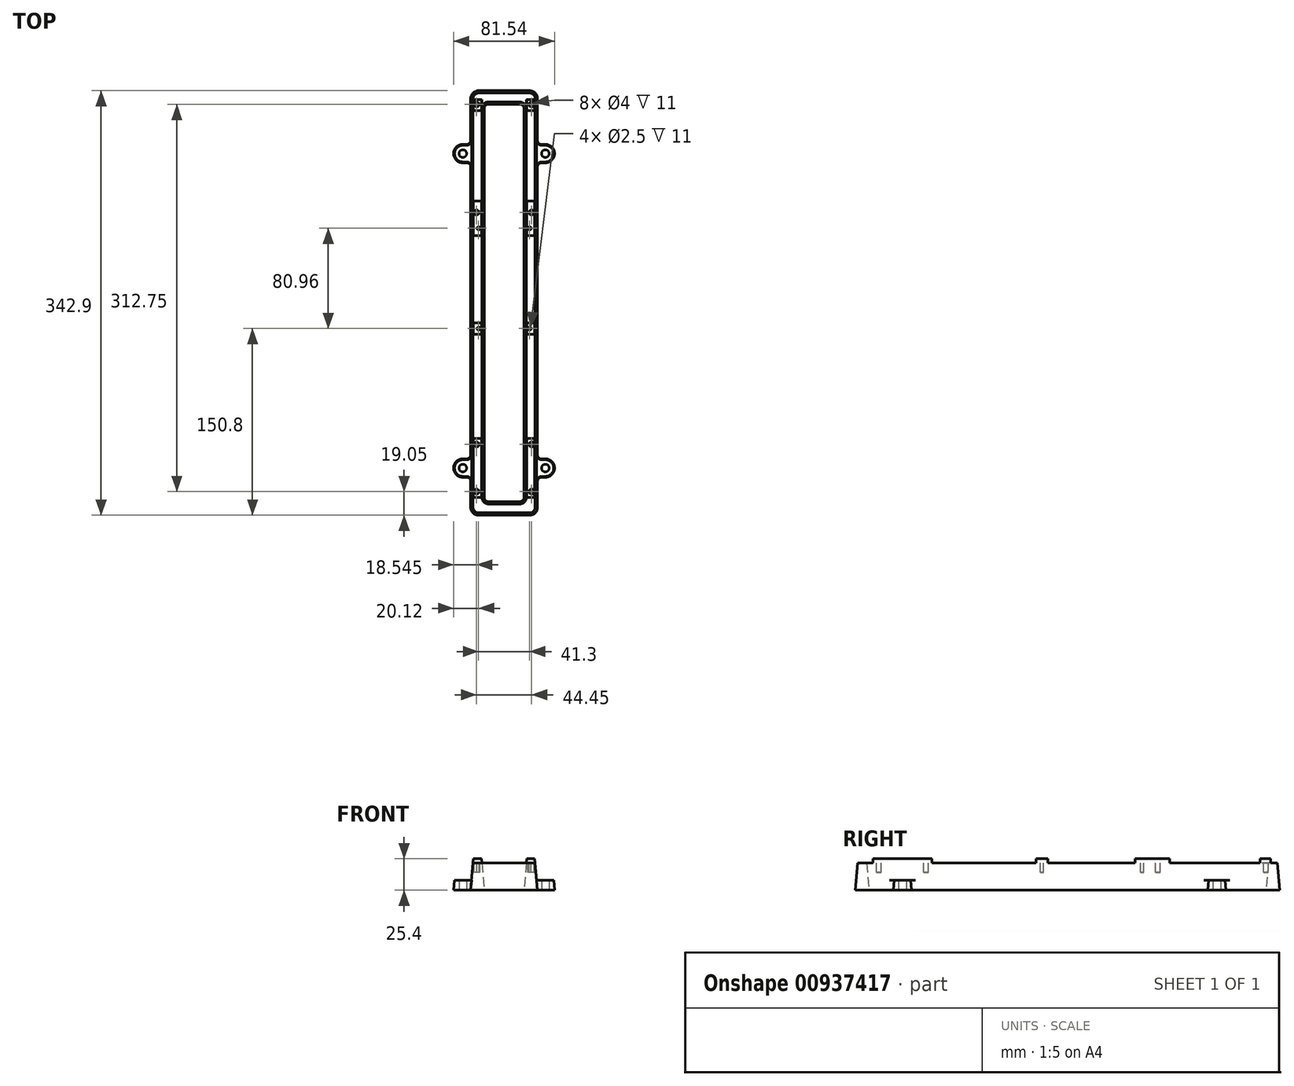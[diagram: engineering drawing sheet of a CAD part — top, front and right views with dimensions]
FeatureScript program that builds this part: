
annotation { "Feature Type Name" : "Feature", "Feature Type Description" : "" }
export const myFeature = defineFeature(function(context is Context, id is Id, definition is map)
    precondition{}
    {
        {
            var Q0;
            Q0=qCreatedBy(makeId("Top.planeOp"),FACE);
            var sketch = newSketch(context, id + "F0", { "sketchPlane" : qUnion([Q0])});
            skLineSegment(sketch, "E0", {"start": v(-33.35, 0) * mm, "end": v(33.35, 0) * mm, "construction": true});
            skLineSegment(sketch, "E1", {"start": v(0, -38.1) * mm, "end": v(0, 304.8) * mm, "construction": true});
            skLineSegment(sketch, "E2", {"start": v(-33.35, 254) * mm, "end": v(33.35, 254) * mm, "construction": true});
            skLineSegment(sketch, "E3.bottom", {"start": v(-20.65, 304.8) * mm, "end": v(20.65, 304.8) * mm});
            skLineSegment(sketch, "E3.top", {"start": v(-20.65, -38.1) * mm, "end": v(20.65, -38.1) * mm});
            skLineSegment(sketch, "E3.left", {"start": v(-27, 298.45) * mm, "end": v(-27, 264.62) * mm});
            skLineSegment(sketch, "E3.right", {"start": v(27, 298.45) * mm, "end": v(27, 264.62) * mm});
            skLineSegment(sketch, "E4.bottom", {"start": v(-12.8, 293.8) * mm, "end": v(12.8, 293.8) * mm});
            skLineSegment(sketch, "E4.top", {"start": v(-12.8, -27.1) * mm, "end": v(12.8, -27.1) * mm});
            skLineSegment(sketch, "E4.left", {"start": v(-16, 290.6) * mm, "end": v(-16, -23.9) * mm});
            skLineSegment(sketch, "E4.right", {"start": v(16, 290.6) * mm, "end": v(16, -23.9) * mm});
            skLineSegment(sketch, "E5", {"start": v(-30.2, 261.43) * mm, "end": v(-33.35, 261.43) * mm});
            skLineSegment(sketch, "E6", {"start": v(-33.35, 246.57) * mm, "end": v(-30.2, 246.57) * mm});
            skLineSegment(sketch, "E7", {"start": v(30.2, 246.57) * mm, "end": v(33.35, 246.57) * mm});
            skLineSegment(sketch, "E8", {"start": v(33.35, 261.43) * mm, "end": v(30.2, 261.43) * mm});
            skLineSegment(sketch, "E9.trimOffspring", {"start": v(-27, 243.37) * mm, "end": v(-27, 10.62) * mm});
            skLineSegment(sketch, "E10.trimOffspring", {"start": v(27, 243.37) * mm, "end": v(27, 10.62) * mm});
            skArc(sketch, "E11", {"start": v(-33.35, 261.43) * mm, "mid": v(-40.78, 254) * mm, "end": v(-33.35, 246.57) * mm});
            skPoint(sketch, "E12.end.orphan", {"position": v(-39.7, 246.57) * mm});
            skArc(sketch, "E13", {"start": v(33.35, 246.57) * mm, "mid": v(40.78, 254) * mm, "end": v(33.35, 261.43) * mm});
            skLineSegment(sketch, "E14", {"start": v(-33.35, 7.42) * mm, "end": v(-30.2, 7.42) * mm});
            skLineSegment(sketch, "E15", {"start": v(30.2, 7.42) * mm, "end": v(33.35, 7.43) * mm});
            skLineSegment(sketch, "E16", {"start": v(33.35, -7.43) * mm, "end": v(30.2, -7.43) * mm});
            skLineSegment(sketch, "E17", {"start": v(-30.2, -7.42) * mm, "end": v(-33.35, -7.42) * mm});
            skArc(sketch, "E18", {"start": v(-33.35, -7.42) * mm, "mid": v(-40.78, 0) * mm, "end": v(-33.35, 7.42) * mm});
            skArc(sketch, "E19", {"start": v(33.35, 7.43) * mm, "mid": v(40.78, 0) * mm, "end": v(33.35, -7.43) * mm});
            skLineSegment(sketch, "E20.trimOffspring", {"start": v(-27, -10.62) * mm, "end": v(-27, -31.75) * mm});
            skLineSegment(sketch, "E21.trimOffspring", {"start": v(27, -10.62) * mm, "end": v(27, -31.75) * mm});
            skPoint(sketch, "E22.visualSharp", {"position": v(27, -38.1) * mm});
            skArc(sketch, "E22.filletArc", {"start": v(20.65, -38.1) * mm, "mid": v(25.14, -36.24) * mm, "end": v(27, -31.75) * mm});
            skPoint(sketch, "E23.visualSharp", {"position": v(-27, -38.1) * mm});
            skArc(sketch, "E23.filletArc", {"start": v(-27, -31.75) * mm, "mid": v(-25.14, -36.24) * mm, "end": v(-20.65, -38.1) * mm});
            skPoint(sketch, "E24.visualSharp", {"position": v(-27, 304.8) * mm});
            skArc(sketch, "E24.filletArc", {"start": v(-20.65, 304.8) * mm, "mid": v(-25.14, 302.94) * mm, "end": v(-27, 298.45) * mm});
            skPoint(sketch, "E25.visualSharp", {"position": v(27, 304.8) * mm});
            skArc(sketch, "E25.filletArc", {"start": v(27, 298.45) * mm, "mid": v(25.14, 302.94) * mm, "end": v(20.65, 304.8) * mm});
            skPoint(sketch, "E26.visualSharp", {"position": v(16, 293.8) * mm});
            skArc(sketch, "E26.filletArc", {"start": v(16, 290.6) * mm, "mid": v(15.06, 292.86) * mm, "end": v(12.8, 293.8) * mm});
            skPoint(sketch, "E27.visualSharp", {"position": v(-16, 293.8) * mm});
            skArc(sketch, "E27.filletArc", {"start": v(-12.8, 293.8) * mm, "mid": v(-15.06, 292.86) * mm, "end": v(-16, 290.6) * mm});
            skPoint(sketch, "E28.visualSharp", {"position": v(-27, 246.57) * mm});
            skArc(sketch, "E28.filletArc", {"start": v(-27, 243.37) * mm, "mid": v(-27.94, 245.64) * mm, "end": v(-30.2, 246.57) * mm});
            skPoint(sketch, "E29.visualSharp", {"position": v(-27, 261.43) * mm});
            skArc(sketch, "E29.filletArc", {"start": v(-30.2, 261.43) * mm, "mid": v(-27.94, 262.36) * mm, "end": v(-27, 264.62) * mm});
            skPoint(sketch, "E30.visualSharp", {"position": v(27, 261.43) * mm});
            skArc(sketch, "E30.filletArc", {"start": v(27, 264.62) * mm, "mid": v(27.94, 262.36) * mm, "end": v(30.2, 261.43) * mm});
            skPoint(sketch, "E31.visualSharp", {"position": v(27, 246.57) * mm});
            skArc(sketch, "E31.filletArc", {"start": v(30.2, 246.57) * mm, "mid": v(27.94, 245.64) * mm, "end": v(27, 243.37) * mm});
            skPoint(sketch, "E32.visualSharp", {"position": v(-16, -27.1) * mm});
            skArc(sketch, "E32.filletArc", {"start": v(-16, -23.9) * mm, "mid": v(-15.06, -26.16) * mm, "end": v(-12.8, -27.1) * mm});
            skPoint(sketch, "E33.visualSharp", {"position": v(16, -27.1) * mm});
            skArc(sketch, "E33.filletArc", {"start": v(12.8, -27.1) * mm, "mid": v(15.06, -26.16) * mm, "end": v(16, -23.9) * mm});
            skPoint(sketch, "E34.visualSharp", {"position": v(27, -7.43) * mm});
            skArc(sketch, "E34.filletArc", {"start": v(30.2, -7.43) * mm, "mid": v(27.94, -8.36) * mm, "end": v(27, -10.62) * mm});
            skPoint(sketch, "E35.visualSharp", {"position": v(27, 7.42) * mm});
            skArc(sketch, "E35.filletArc", {"start": v(27, 10.62) * mm, "mid": v(27.94, 8.36) * mm, "end": v(30.2, 7.43) * mm});
            skPoint(sketch, "E36.visualSharp", {"position": v(-27, 7.42) * mm});
            skArc(sketch, "E36.filletArc", {"start": v(-30.2, 7.43) * mm, "mid": v(-27.94, 8.36) * mm, "end": v(-27, 10.62) * mm});
            skPoint(sketch, "E37.visualSharp", {"position": v(-27, -7.42) * mm});
            skArc(sketch, "E37.filletArc", {"start": v(-27, -10.62) * mm, "mid": v(-27.94, -8.36) * mm, "end": v(-30.2, -7.42) * mm});
            skSolve(sketch);
        }
        {
            var Q0;
            Q0 = qSketchRegion(id + "F0", true);
            extrude(context, id + "F1", {"entities" : qUnion([Q0]), "depth" : 25.4 * mm, "offsetDistance" : 25 * mm, "hasDraft" : true, "draftAngle" : 5 * degree, "draftPullDirection" : true});
        }
        {
            var Q0;
            Q0=qCreatedBy(makeId("Front.planeOp"),FACE);
            var sketch = newSketch(context, id + "F2", { "sketchPlane" : qUnion([Q0])});
            skLineSegment(sketch, "E38.0", {"start": v(-24.78, 25.4) * mm, "end": v(-26.3, 8.1) * mm});
            skLineSegment(sketch, "E39.0", {"start": v(24.78, 25.4) * mm, "end": v(26.3, 8.1) * mm});
            skLineSegment(sketch, "E40.0", {"start": v(-38.55, 25.4) * mm, "end": v(-24.78, 25.4) * mm});
            skLineSegment(sketch, "E41", {"start": v(38.55, 25.4) * mm, "end": v(40.07, 8.1) * mm});
            skLineSegment(sketch, "E42", {"start": v(-40.07, 8.1) * mm, "end": v(-38.55, 25.4) * mm});
            skLineSegment(sketch, "E43", {"start": v(40.07, 8.1) * mm, "end": v(26.3, 8.1) * mm});
            skPoint(sketch, "E44.orphan", {"position": v(27, 0) * mm});
            skLineSegment(sketch, "E45.trimOffspring", {"start": v(-26.3, 8.1) * mm, "end": v(-40.07, 8.1) * mm});
            skPoint(sketch, "E46.orphan", {"position": v(-27, 0) * mm});
            skPoint(sketch, "E47.orphan", {"position": v(-20.65, 25.4) * mm});
            skPoint(sketch, "E48.orphan", {"position": v(20.65, 25.4) * mm});
            skLineSegment(sketch, "E49.trimOffspring", {"start": v(24.78, 25.4) * mm, "end": v(38.55, 25.4) * mm});
            skSolve(sketch);
        }
        {
            var Q0;
            Q0 = qSketchRegion(id + "F2", true);
            extrude(context, id + "F3", {"entities" : qUnion([Q0]), "operationType" : NewBodyOperationType.REMOVE, "endBound" : BoundingType.THROUGH_ALL, "oppositeDirection" : true, "depth" : 25 * mm, "offsetDistance" : 25 * mm, "hasSecondDirection" : true, "secondDirectionBound" : SecondDirectionBoundingType.THROUGH_ALL, "secondDirectionOppositeDirection" : false, "secondDirectionDepth" : 25 * mm});
        }
        {
            var Q0;
            Q0=qCreatedBy(makeId("Right.planeOp"),FACE);
            var sketch = newSketch(context, id + "F4", { "sketchPlane" : qUnion([Q0])});
            skLineSegment(sketch, "E50.0", {"start": v(187.8, 25.4) * mm, "end": v(117.38, 25.4) * mm});
            skLineSegment(sketch, "E51", {"start": v(-23.8, 25.4) * mm, "end": v(-23.8, 22) * mm});
            skLineSegment(sketch, "E52", {"start": v(-23.8, 22) * mm, "end": v(-36.18, 22) * mm});
            skLineSegment(sketch, "E53", {"start": v(23.8, 25.4) * mm, "end": v(23.8, 22) * mm});
            skLineSegment(sketch, "E54", {"start": v(23.8, 22) * mm, "end": v(108.03, 22) * mm});
            skLineSegment(sketch, "E55", {"start": v(0, 25.4) * mm, "end": v(0, 0) * mm, "construction": true});
            skLineSegment(sketch, "E56.0", {"start": v(-35.88, 25.4) * mm, "end": v(-36.18, 22) * mm});
            skPoint(sketch, "E57.orphan", {"position": v(-38.1, 0) * mm});
            skPoint(sketch, "E58.orphan", {"position": v(-31.75, 25.4) * mm});
            skLineSegment(sketch, "E59.trimOffspring", {"start": v(-23.8, 25.4) * mm, "end": v(-35.88, 25.4) * mm});
            skLineSegment(sketch, "E60", {"start": v(112.7, 25.4) * mm, "end": v(112.7, 0) * mm, "construction": true});
            skLineSegment(sketch, "E61", {"start": v(117.38, 25.4) * mm, "end": v(117.38, 22) * mm});
            skLineSegment(sketch, "E62", {"start": v(108.03, 22) * mm, "end": v(108.03, 25.4) * mm});
            skLineSegment(sketch, "E63", {"start": v(108.03, 25.4) * mm, "end": v(23.8, 25.4) * mm});
            skLineSegment(sketch, "E64", {"start": v(187.8, 22) * mm, "end": v(117.38, 22) * mm});
            skLineSegment(sketch, "E65", {"start": v(187.8, 22) * mm, "end": v(187.8, 25.4) * mm});
            skPoint(sketch, "E66.orphan", {"position": v(298.45, 25.4) * mm});
            skLineSegment(sketch, "E67", {"start": v(206.4, 25.52) * mm, "end": v(206.4, 0) * mm, "construction": true});
            skSolve(sketch);
        }
        {
            var Q0;
            Q0 = qSketchRegion(id + "F4", true);
            extrude(context, id + "F5", {"entities" : qUnion([Q0]), "operationType" : NewBodyOperationType.REMOVE, "endBound" : BoundingType.THROUGH_ALL, "oppositeDirection" : true, "depth" : 25 * mm, "offsetDistance" : 25 * mm, "hasSecondDirection" : true, "secondDirectionBound" : SecondDirectionBoundingType.THROUGH_ALL, "secondDirectionOppositeDirection" : false, "secondDirectionDepth" : 25 * mm});
        }
        {
            var Q0;
            Q0=qCreatedBy(makeId("Right.planeOp"),FACE);
            var sketch = newSketch(context, id + "F6", { "sketchPlane" : qUnion([Q0])});
            skLineSegment(sketch, "E68.0", {"start": v(187.8, 22) * mm, "end": v(117.38, 22) * mm});
            skLineSegment(sketch, "E69.0", {"start": v(302.58, 25.4) * mm, "end": v(297.5, 25.4) * mm});
            skLineSegment(sketch, "E70", {"start": v(215.8, 25.4) * mm, "end": v(215.8, 22) * mm});
            skLineSegment(sketch, "E71", {"start": v(297.5, 25.4) * mm, "end": v(297.5, 22) * mm});
            skLineSegment(sketch, "E72", {"start": v(302.88, 22) * mm, "end": v(297.5, 22) * mm});
            skLineSegment(sketch, "E73", {"start": v(288.8, 22) * mm, "end": v(288.8, 25.4) * mm});
            skPoint(sketch, "E74.orphan", {"position": v(298.45, 25.4) * mm});
            skLineSegment(sketch, "E75.trimOffspring", {"start": v(288.8, 25.4) * mm, "end": v(187.8, 25.4) * mm});
            skLineSegment(sketch, "E76.trimOffspring", {"start": v(288.8, 22) * mm, "end": v(215.8, 22) * mm});
            skLineSegment(sketch, "E77.0", {"start": v(302.58, 25.4) * mm, "end": v(302.88, 22) * mm});
            skPoint(sketch, "E78.orphan", {"position": v(304.8, 0) * mm});
            skLineSegment(sketch, "E79", {"start": v(293.7, 25.53) * mm, "end": v(293.7, 22) * mm, "construction": true});
            skSolve(sketch);
        }
        {
            var Q0;
            Q0 = qSketchRegion(id + "F6", true);
            extrude(context, id + "F7", {"entities" : qUnion([Q0]), "operationType" : NewBodyOperationType.REMOVE, "endBound" : BoundingType.THROUGH_ALL, "oppositeDirection" : true, "depth" : 25 * mm, "offsetDistance" : 25 * mm, "hasSecondDirection" : true, "secondDirectionBound" : SecondDirectionBoundingType.THROUGH_ALL, "secondDirectionOppositeDirection" : false, "secondDirectionDepth" : 25 * mm});
        }
        {
            var Q0;
            {var subQ2=sQuery(id+"F0.wireOp",EDGE,"E3.left");Q0=makeQuery(id+"F7.boolean.opBoolean","COPY",FACE,{"disambiguationData":[TD([makeQuery(id+"F1.opExtrude","SWEPT_FACE",FACE,{"disambiguationData":[OSD([subQ2])]})])],"derivedFrom":makeQuery(id+"F7.opExtrude","SWEPT_FACE",FACE,{"disambiguationData":[OSD([sQuery(id+"F6.wireOp",EDGE,"E73")])]})});}
            var sketch = newSketch(context, id + "F8", { "sketchPlane" : qUnion([Q0])});
            skLineSegment(sketch, "E80.0", {"start": v(-17.92, 22) * mm, "end": v(-18.22, 25.4) * mm});
            skLineSegment(sketch, "E81.0", {"start": v(17.92, 22) * mm, "end": v(18.22, 25.4) * mm});
            skLineSegment(sketch, "E82.0", {"start": v(-18.22, 25.4) * mm, "end": v(18.22, 25.4) * mm});
            skLineSegment(sketch, "E83.0", {"start": v(-17.92, 22) * mm, "end": v(17.92, 22) * mm});
            skPoint(sketch, "E84.orphan", {"position": v(-20.65, 22) * mm});
            skPoint(sketch, "E85.orphan", {"position": v(20.65, 22) * mm});
            skPoint(sketch, "E86.orphan", {"position": v(12.8, 25.4) * mm});
            skPoint(sketch, "E87.orphan", {"position": v(-12.8, 25.4) * mm});
            skSolve(sketch);
        }
        {
            var Q0;
            Q0 = qSketchRegion(id + "F8", true);
            extrude(context, id + "F9", {"entities" : qUnion([Q0]), "operationType" : NewBodyOperationType.REMOVE, "endBound" : BoundingType.THROUGH_ALL, "oppositeDirection" : true, "depth" : 25 * mm, "offsetDistance" : 25 * mm});
        }
        {
            var Q0;
            Q0=makeQuery(id+"F1.opExtrude","CAP_FACE",FACE,{"disambiguationData":[OSD([sQuery(id+"F0.wireOp",EDGE,"E3.bottom"),sQuery(id+"F0.wireOp",EDGE,"E3.top"),sQuery(id+"F0.wireOp",EDGE,"E3.left"),sQuery(id+"F0.wireOp",EDGE,"E3.right"),sQuery(id+"F0.wireOp",EDGE,"E4.bottom"),sQuery(id+"F0.wireOp",EDGE,"E4.top"),sQuery(id+"F0.wireOp",EDGE,"E4.left"),sQuery(id+"F0.wireOp",EDGE,"E4.right"),sQuery(id+"F0.wireOp",EDGE,"E5"),sQuery(id+"F0.wireOp",EDGE,"E6"),sQuery(id+"F0.wireOp",EDGE,"E7"),sQuery(id+"F0.wireOp",EDGE,"E8"),sQuery(id+"F0.wireOp",EDGE,"E9.trimOffspring"),sQuery(id+"F0.wireOp",EDGE,"E10.trimOffspring"),sQuery(id+"F0.wireOp",EDGE,"E11"),sQuery(id+"F0.wireOp",EDGE,"E13"),sQuery(id+"F0.wireOp",EDGE,"E14"),sQuery(id+"F0.wireOp",EDGE,"E15"),sQuery(id+"F0.wireOp",EDGE,"E16"),sQuery(id+"F0.wireOp",EDGE,"E17"),sQuery(id+"F0.wireOp",EDGE,"E18"),sQuery(id+"F0.wireOp",EDGE,"E19"),sQuery(id+"F0.wireOp",EDGE,"E20.trimOffspring"),sQuery(id+"F0.wireOp",EDGE,"E21.trimOffspring"),sQuery(id+"F0.wireOp",EDGE,"E22.filletArc"),sQuery(id+"F0.wireOp",EDGE,"E23.filletArc"),sQuery(id+"F0.wireOp",EDGE,"E24.filletArc"),sQuery(id+"F0.wireOp",EDGE,"E25.filletArc"),sQuery(id+"F0.wireOp",EDGE,"E26.filletArc"),sQuery(id+"F0.wireOp",EDGE,"E27.filletArc"),sQuery(id+"F0.wireOp",EDGE,"E28.filletArc"),sQuery(id+"F0.wireOp",EDGE,"E29.filletArc"),sQuery(id+"F0.wireOp",EDGE,"E30.filletArc"),sQuery(id+"F0.wireOp",EDGE,"E31.filletArc"),sQuery(id+"F0.wireOp",EDGE,"E32.filletArc"),sQuery(id+"F0.wireOp",EDGE,"E33.filletArc"),sQuery(id+"F0.wireOp",EDGE,"E34.filletArc"),sQuery(id+"F0.wireOp",EDGE,"E35.filletArc"),sQuery(id+"F0.wireOp",EDGE,"E36.filletArc"),sQuery(id+"F0.wireOp",EDGE,"E37.filletArc")])],"isStart":true});
            var sketch = newSketch(context, id + "F10", { "sketchPlane" : qUnion([Q0])});
            skCircle(sketch, "E88", {"center": v(-33.35, 0) * mm, "radius": 3.1 * mm});
            skCircle(sketch, "E89", {"center": v(33.35, 0) * mm, "radius": 3.1 * mm});
            skCircle(sketch, "E90", {"center": v(-33.35, -254) * mm, "radius": 3.1 * mm});
            skCircle(sketch, "E91", {"center": v(33.35, -254) * mm, "radius": 3.1 * mm});
            skSolve(sketch);
        }
        {
            var Q0;
            Q0 = qSketchRegion(id + "F10", true);
            extrude(context, id + "F11", {"entities" : qUnion([Q0]), "operationType" : NewBodyOperationType.REMOVE, "endBound" : BoundingType.THROUGH_ALL, "oppositeDirection" : true, "depth" : 25 * mm, "offsetDistance" : 25 * mm});
        }
        {
            var Q0;
            {var subQ0=sQuery(id+"F0.wireOp",EDGE,"E4.left");var subQ1=sQuery(id+"F0.wireOp",EDGE,"E20.trimOffspring");var subQ2=sQuery(id+"F0.wireOp",EDGE,"E9.trimOffspring");var subQ3=sQuery(id+"F0.wireOp",EDGE,"E3.left");Q0=makeQuery(id+"F5.boolean.opBoolean","SPLIT",FACE,{"disambiguationData":[TD([makeQuery(id+"F1.opExtrude","SWEPT_FACE",FACE,{"disambiguationData":[OSD([subQ3])]}),makeQuery(id+"F1.opExtrude","SWEPT_FACE",FACE,{"disambiguationData":[OSD([subQ0])]}),makeQuery(id+"F1.opExtrude","SWEPT_FACE",FACE,{"disambiguationData":[OSD([subQ2])]}),makeQuery(id+"F1.opExtrude","SWEPT_FACE",FACE,{"disambiguationData":[OSD([subQ1])]}),makeQuery(id+"F5.opExtrude","SWEPT_FACE",FACE,{"disambiguationData":[OSD([sQuery(id+"F4.wireOp",EDGE,"E51")])]}),makeQuery(id+"F5.opExtrude","SWEPT_FACE",FACE,{"disambiguationData":[OSD([sQuery(id+"F4.wireOp",EDGE,"E53")])]})])],"derivedFrom":makeQuery(id+"F1.opExtrude","CAP_FACE",FACE,{"disambiguationData":[OSD([sQuery(id+"F0.wireOp",EDGE,"E3.bottom"),sQuery(id+"F0.wireOp",EDGE,"E3.top"),subQ3,sQuery(id+"F0.wireOp",EDGE,"E3.right"),sQuery(id+"F0.wireOp",EDGE,"E4.bottom"),sQuery(id+"F0.wireOp",EDGE,"E4.top"),subQ0,sQuery(id+"F0.wireOp",EDGE,"E4.right"),sQuery(id+"F0.wireOp",EDGE,"E5"),sQuery(id+"F0.wireOp",EDGE,"E6"),sQuery(id+"F0.wireOp",EDGE,"E7"),sQuery(id+"F0.wireOp",EDGE,"E8"),subQ2,sQuery(id+"F0.wireOp",EDGE,"E10.trimOffspring"),sQuery(id+"F0.wireOp",EDGE,"E11"),sQuery(id+"F0.wireOp",EDGE,"E13"),sQuery(id+"F0.wireOp",EDGE,"E14"),sQuery(id+"F0.wireOp",EDGE,"E15"),sQuery(id+"F0.wireOp",EDGE,"E16"),sQuery(id+"F0.wireOp",EDGE,"E17"),sQuery(id+"F0.wireOp",EDGE,"E18"),sQuery(id+"F0.wireOp",EDGE,"E19"),subQ1,sQuery(id+"F0.wireOp",EDGE,"E21.trimOffspring"),sQuery(id+"F0.wireOp",EDGE,"E22.filletArc"),sQuery(id+"F0.wireOp",EDGE,"E23.filletArc"),sQuery(id+"F0.wireOp",EDGE,"E24.filletArc"),sQuery(id+"F0.wireOp",EDGE,"E25.filletArc"),sQuery(id+"F0.wireOp",EDGE,"E26.filletArc"),sQuery(id+"F0.wireOp",EDGE,"E27.filletArc"),sQuery(id+"F0.wireOp",EDGE,"E28.filletArc"),sQuery(id+"F0.wireOp",EDGE,"E29.filletArc"),sQuery(id+"F0.wireOp",EDGE,"E30.filletArc"),sQuery(id+"F0.wireOp",EDGE,"E31.filletArc"),sQuery(id+"F0.wireOp",EDGE,"E32.filletArc"),sQuery(id+"F0.wireOp",EDGE,"E33.filletArc"),sQuery(id+"F0.wireOp",EDGE,"E34.filletArc"),sQuery(id+"F0.wireOp",EDGE,"E35.filletArc"),sQuery(id+"F0.wireOp",EDGE,"E36.filletArc"),sQuery(id+"F0.wireOp",EDGE,"E37.filletArc")])],"isStart":false})});}
            var sketch = newSketch(context, id + "F12", { "sketchPlane" : qUnion([Q0])});
            skCircle(sketch, "E92", {"center": v(22.23, -19.05) * mm, "radius": 2 * mm});
            skCircle(sketch, "E93", {"center": v(22.23, 19.05) * mm, "radius": 2 * mm});
            skCircle(sketch, "E94", {"center": v(-22.23, 19.05) * mm, "radius": 2 * mm});
            skCircle(sketch, "E95", {"center": v(-22.23, -19.05) * mm, "radius": 2 * mm});
            skLineSegment(sketch, "E96", {"start": v(-22.23, -19.05) * mm, "end": v(-22.23, 293.7) * mm, "construction": true});
            skLineSegment(sketch, "E97", {"start": v(22.23, -19.05) * mm, "end": v(22.23, 293.7) * mm, "construction": true});
            skLineSegment(sketch, "E98", {"start": v(22.23, 293.7) * mm, "end": v(-22.23, 293.7) * mm, "construction": true});
            skLineSegment(sketch, "E99", {"start": v(22.23, 206.4) * mm, "end": v(-22.23, 206.4) * mm, "construction": true});
            skCircle(sketch, "E100", {"center": v(22.23, 293.7) * mm, "radius": 2 * mm});
            skCircle(sketch, "E101", {"center": v(22.23, 206.4) * mm, "radius": 2 * mm});
            skCircle(sketch, "E102", {"center": v(-22.23, 206.4) * mm, "radius": 2 * mm});
            skCircle(sketch, "E103", {"center": v(-22.23, 293.7) * mm, "radius": 2 * mm});
            skLineSegment(sketch, "E104", {"start": v(20.65, 193.66) * mm, "end": v(20.65, 112.7) * mm, "construction": true});
            skLineSegment(sketch, "E105", {"start": v(20.65, 112.7) * mm, "end": v(-20.65, 112.7) * mm, "construction": true});
            skLineSegment(sketch, "E106", {"start": v(-20.65, 112.7) * mm, "end": v(-20.65, 193.66) * mm, "construction": true});
            skLineSegment(sketch, "E107", {"start": v(-20.65, 193.66) * mm, "end": v(20.65, 193.66) * mm, "construction": true});
            skCircle(sketch, "E108", {"center": v(20.65, 193.66) * mm, "radius": 1.25 * mm});
            skCircle(sketch, "E109", {"center": v(20.65, 112.7) * mm, "radius": 1.25 * mm});
            skCircle(sketch, "E110", {"center": v(-20.65, 112.7) * mm, "radius": 1.25 * mm});
            skCircle(sketch, "E111", {"center": v(-20.65, 193.66) * mm, "radius": 1.25 * mm});
            skSolve(sketch);
        }
        {
            var Q0;
            Q0 = qSketchRegion(id + "F12", true);
            extrude(context, id + "F13", {"entities" : qUnion([Q0]), "operationType" : NewBodyOperationType.REMOVE, "oppositeDirection" : true, "depth" : 11 * mm, "offsetDistance" : 25 * mm});
        }
    });
